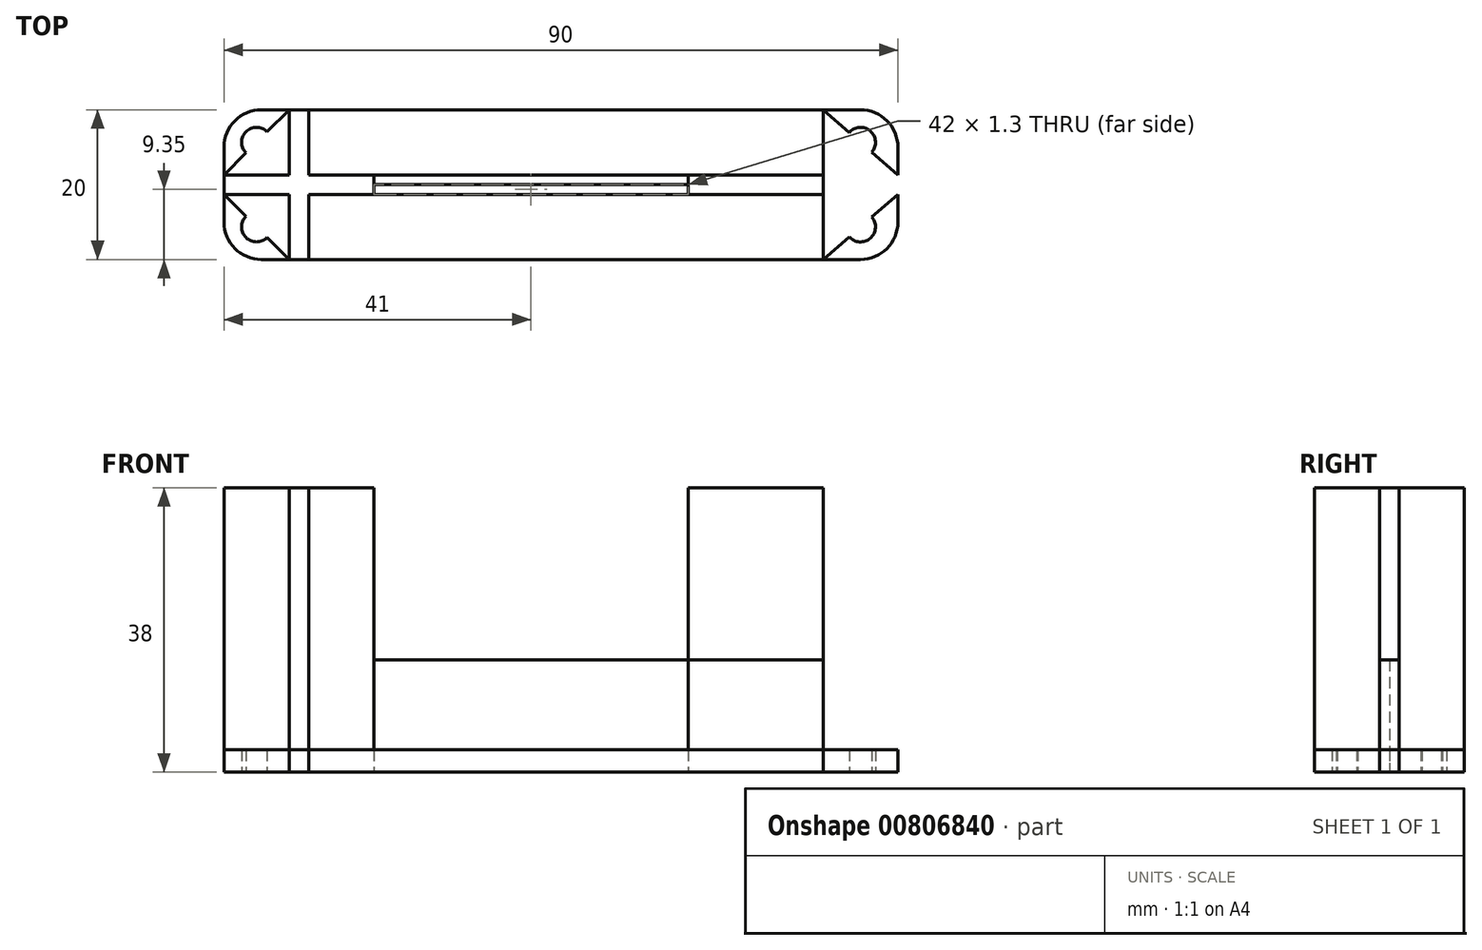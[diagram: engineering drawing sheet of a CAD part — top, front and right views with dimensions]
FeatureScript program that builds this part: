
annotation { "Feature Type Name" : "Feature", "Feature Type Description" : "" }
export const myFeature = defineFeature(function(context is Context, id is Id, definition is map)
    precondition{}
    {
        {
            var Q0;
            Q0=qCreatedBy(makeId("Top.planeOp"),FACE);
            var sketch = newSketch(context, id + "F0", { "sketchPlane" : qUnion([Q0])});
            skLineSegment(sketch, "E0.bottom", {"start": v(10, 1.3) * mm, "end": v(-10, 1.3) * mm});
            skLineSegment(sketch, "E0.top", {"start": v(10, -1.3) * mm, "end": v(-10, -1.3) * mm});
            skLineSegment(sketch, "E0.left", {"start": v(10, 1.3) * mm, "end": v(10, -1.3) * mm});
            skLineSegment(sketch, "E0.right", {"start": v(-10, 1.3) * mm, "end": v(-10, -1.3) * mm});
            skPoint(sketch, "E0.middle", {"position": v(0, 0) * mm});
            skLineSegment(sketch, "E1.bottom", {"start": v(1.3, 10) * mm, "end": v(-1.3, 10) * mm});
            skLineSegment(sketch, "E1.top", {"start": v(1.3, -10) * mm, "end": v(-1.3, -10) * mm});
            skLineSegment(sketch, "E1.left", {"start": v(1.3, 10) * mm, "end": v(1.3, -10) * mm});
            skLineSegment(sketch, "E1.right", {"start": v(-1.3, 10) * mm, "end": v(-1.3, -10) * mm});
            skLineSegment(sketch, "E2.bottom", {"start": v(0, 0) * mm, "end": v(80, 0) * mm});
            skLineSegment(sketch, "E2.top", {"start": v(0, 1.3) * mm, "end": v(80, 1.3) * mm});
            skLineSegment(sketch, "E2.left", {"start": v(0, 0) * mm, "end": v(0, 1.3) * mm});
            skLineSegment(sketch, "E2.right", {"start": v(80, 0) * mm, "end": v(80, 1.3) * mm});
            skLineSegment(sketch, "E3.top", {"start": v(0, -1.3) * mm, "end": v(80, -1.3) * mm});
            skLineSegment(sketch, "E3.left", {"start": v(0, 0) * mm, "end": v(0, -1.3) * mm});
            skLineSegment(sketch, "E3.right", {"start": v(80, 0) * mm, "end": v(80, -1.3) * mm});
            skLineSegment(sketch, "E4.bottom", {"start": v(-5, -10) * mm, "end": v(75, -10) * mm});
            skLineSegment(sketch, "E4.top", {"start": v(-5, 10) * mm, "end": v(75, 10) * mm});
            skLineSegment(sketch, "E4.left", {"start": v(-10, -5) * mm, "end": v(-10, 5) * mm});
            skLineSegment(sketch, "E4.right", {"start": v(80, -10) * mm, "end": v(80, 10) * mm});
            skLineSegment(sketch, "E5.bottom", {"start": v(80, -10) * mm, "end": v(70, -10) * mm});
            skLineSegment(sketch, "E5.top", {"start": v(80, 10) * mm, "end": v(70, 10) * mm});
            skLineSegment(sketch, "E5.left", {"start": v(80, -5) * mm, "end": v(80, 5) * mm});
            skLineSegment(sketch, "E5.right", {"start": v(70, -10) * mm, "end": v(70, 10) * mm});
            skArc(sketch, "E6", {"start": v(1.3, 10) * mm, "mid": v(35.65, 3.3) * mm, "end": v(70, 10) * mm});
            skArc(sketch, "E7", {"start": v(70, -10) * mm, "mid": v(35.65, -3.3) * mm, "end": v(1.3, -10) * mm});
            skLineSegment(sketch, "E8", {"start": v(35.65, -3.3) * mm, "end": v(35.65, -1.3) * mm});
            skLineSegment(sketch, "E9", {"start": v(35.65, 3.3) * mm, "end": v(35.65, 1.3) * mm});
            skLineSegment(sketch, "E10", {"start": v(-10, 1.3) * mm, "end": v(-1.3, 10) * mm});
            skCircle(sketch, "E11", {"center": v(-5.65, 5.65) * mm, "radius": 2 * mm});
            skLineSegment(sketch, "E12", {"start": v(-10, -1.3) * mm, "end": v(-1.3, -10) * mm});
            skLineSegment(sketch, "E13", {"start": v(70, 10) * mm, "end": v(80, 1.3) * mm});
            skLineSegment(sketch, "E14", {"start": v(70, -10) * mm, "end": v(80, -1.3) * mm});
            skCircle(sketch, "E15", {"center": v(-5.65, -5.65) * mm, "radius": 2 * mm});
            skPoint(sketch, "E16.visualSharp", {"position": v(-10, 10) * mm});
            skArc(sketch, "E16.filletArc", {"start": v(-5, 10) * mm, "mid": v(-8.54, 8.54) * mm, "end": v(-10, 5) * mm});
            skPoint(sketch, "E17.visualSharp", {"position": v(-10, -10) * mm});
            skArc(sketch, "E17.filletArc", {"start": v(-10, -5) * mm, "mid": v(-8.54, -8.54) * mm, "end": v(-5, -10) * mm});
            skCircle(sketch, "E18", {"center": v(75, 5.65) * mm, "radius": 2 * mm});
            skCircle(sketch, "E19", {"center": v(75, -5.65) * mm, "radius": 2 * mm});
            skPoint(sketch, "E20.visualSharp", {"position": v(80, 10) * mm});
            skArc(sketch, "E20.filletArc", {"start": v(80, 5) * mm, "mid": v(78.54, 8.54) * mm, "end": v(75, 10) * mm});
            skPoint(sketch, "E21.visualSharp", {"position": v(80, -10) * mm});
            skArc(sketch, "E21.filletArc", {"start": v(75, -10) * mm, "mid": v(78.54, -8.54) * mm, "end": v(80, -5) * mm});
            skLineSegment(sketch, "E22", {"start": v(0, -1.3) * mm, "end": v(52, -1.3) * mm});
            skLineSegment(sketch, "E23", {"start": v(52, -1.3) * mm, "end": v(52, 1.3) * mm});
            skSolve(sketch);
        }
        {
            var Q0;
            {var subQ0=sQuery(id+"F0.wireOp",EDGE,"E5.left");var subQ1=sQuery(id+"F0.wireOp",EDGE,"E2.bottom");var subQ2=makeQuery(id+"F0.imprint","INTERSECT",VERTEX,{"derivedFrom":[subQ1,subQ0]});Q0=makeQuery(id+"F0.imprint","IMPRINT",FACE,{"disambiguationData":[TD([[makeQuery(id+"F0.imprint","IMPRINT",EDGE,{"disambiguationData":[TD([[subQ2,1.0]])],"derivedFrom":subQ1}),-1.0]])]});}
            var Q1;
            {var subQ0=sQuery(id+"F0.wireOp",EDGE,"E5.left");var subQ5=sQuery(id+"F0.wireOp",EDGE,"E2.bottom");var subQ6=makeQuery(id+"F0.imprint","INTERSECT",VERTEX,{"derivedFrom":[subQ5,subQ0]});Q1=makeQuery(id+"F0.imprint","IMPRINT",FACE,{"disambiguationData":[TD([[makeQuery(id+"F0.imprint","IMPRINT",EDGE,{"disambiguationData":[TD([[subQ6,1.0]])],"derivedFrom":subQ5}),1.0]])]});}
            var Q2;
            {var subQ1=sQuery(id+"F0.wireOp",EDGE,"E0.bottom");var subQ7=sQuery(id+"F0.wireOp",EDGE,"E1.right");var subQ9=makeQuery(id+"F0.imprint","INTERSECT",VERTEX,{"derivedFrom":[subQ1,subQ7]});Q2=makeQuery(id+"F0.imprint","IMPRINT",FACE,{"disambiguationData":[TD([[makeQuery(id+"F0.imprint","IMPRINT",EDGE,{"disambiguationData":[TD([[subQ9,1.0]])],"derivedFrom":subQ1}),-1.0]])]});}
            var Q3;
            {var subQ1=sQuery(id+"F0.wireOp",EDGE,"E0.bottom");var subQ3=sQuery(id+"F0.wireOp",EDGE,"E1.right");var subQ4=makeQuery(id+"F0.imprint","INTERSECT",VERTEX,{"derivedFrom":[subQ1,subQ3]});Q3=makeQuery(id+"F0.imprint","IMPRINT",FACE,{"disambiguationData":[TD([[makeQuery(id+"F0.imprint","IMPRINT",EDGE,{"disambiguationData":[TD([[subQ4,-1.0]])],"derivedFrom":subQ3}),-1.0]])]});}
            var Q4;
            {var subQ3=sQuery(id+"F0.wireOp",EDGE,"E1.right");var subQ7=sQuery(id+"F0.wireOp",EDGE,"E0.top");var subQ8=makeQuery(id+"F0.imprint","INTERSECT",VERTEX,{"derivedFrom":[subQ7,subQ3]});Q4=makeQuery(id+"F0.imprint","IMPRINT",FACE,{"disambiguationData":[TD([[makeQuery(id+"F0.imprint","IMPRINT",EDGE,{"disambiguationData":[TD([[subQ8,1.0]])],"derivedFrom":subQ7}),1.0]])]});}
            var Q5;
            {var subQ0=sQuery(id+"F0.wireOp",EDGE,"E22");var subQ1=sQuery(id+"F0.wireOp",EDGE,"E0.left");var subQ2=makeQuery(id+"F0.imprint","INTERSECT",VERTEX,{"derivedFrom":[subQ1,subQ0]});Q5=makeQuery(id+"F0.imprint","IMPRINT",FACE,{"disambiguationData":[TD([[makeQuery(id+"F0.imprint","IMPRINT",EDGE,{"disambiguationData":[TD([[subQ2,1.0]])],"derivedFrom":subQ1}),-1.0]])]});}
            var Q6;
            {var subQ0=sQuery(id+"F0.wireOp",EDGE,"E2.top");var subQ1=sQuery(id+"F0.wireOp",EDGE,"E0.left");var subQ2=makeQuery(id+"F0.imprint","INTERSECT",VERTEX,{"derivedFrom":[subQ1,subQ0]});Q6=makeQuery(id+"F0.imprint","IMPRINT",FACE,{"disambiguationData":[TD([[makeQuery(id+"F0.imprint","IMPRINT",EDGE,{"disambiguationData":[TD([[subQ2,-1.0]])],"derivedFrom":subQ1}),-1.0]])]});}
            var Q7;
            {var subQ5=sQuery(id+"F0.wireOp",EDGE,"E3.left");Q7=makeQuery(id+"F0.imprint","IMPRINT",FACE,{"disambiguationData":[TD([[makeQuery(id+"F0.imprint","IMPRINT",EDGE,{"derivedFrom":subQ5}),1.0]])]});}
            var Q8;
            {var subQ5=sQuery(id+"F0.wireOp",EDGE,"E2.left");Q8=makeQuery(id+"F0.imprint","IMPRINT",FACE,{"disambiguationData":[TD([[makeQuery(id+"F0.imprint","IMPRINT",EDGE,{"derivedFrom":subQ5}),-1.0]])]});}
            var Q9;
            {var subQ0=sQuery(id+"F0.wireOp",EDGE,"E2.left");Q9=makeQuery(id+"F0.imprint","IMPRINT",FACE,{"disambiguationData":[TD([[makeQuery(id+"F0.imprint","IMPRINT",EDGE,{"derivedFrom":subQ0}),1.0]])]});}
            extrude(context, id + "F1", {"entities" : qUnion([Q0, Q1, Q2, Q3, Q4, Q5, Q6, Q7, Q8, Q9]), "depth" : 38 * mm, "offsetDistance" : 25 * mm});
        }
        {
            var Q0;
            {var subQ8=sQuery(id+"F0.wireOp",EDGE,"E17.filletArc");Q0=makeQuery(id+"F0.imprint","IMPRINT",FACE,{"disambiguationData":[TD([[makeQuery(id+"F0.imprint","IMPRINT",EDGE,{"derivedFrom":subQ8}),1.0]])]});}
            var Q1;
            {var subQ0=sQuery(id+"F0.wireOp",EDGE,"E7");var subQ4=makeQuery(id+"F0.imprint","INTERSECT",VERTEX,{"derivedFrom":[subQ0,sQuery(id+"F0.wireOp",EDGE,"E8")]});Q1=makeQuery(id+"F0.imprint","IMPRINT",FACE,{"disambiguationData":[TD([[makeQuery(id+"F0.imprint","IMPRINT",EDGE,{"disambiguationData":[TD([[subQ4,-1.0]])],"derivedFrom":subQ0}),1.0]])]});}
            var Q2;
            {var subQ8=sQuery(id+"F0.wireOp",EDGE,"E16.filletArc");Q2=makeQuery(id+"F0.imprint","IMPRINT",FACE,{"disambiguationData":[TD([[makeQuery(id+"F0.imprint","IMPRINT",EDGE,{"derivedFrom":subQ8}),1.0]])]});}
            var Q3;
            {var subQ0=sQuery(id+"F0.wireOp",EDGE,"E6");var subQ4=makeQuery(id+"F0.imprint","INTERSECT",VERTEX,{"derivedFrom":[subQ0,sQuery(id+"F0.wireOp",EDGE,"E9")]});Q3=makeQuery(id+"F0.imprint","IMPRINT",FACE,{"disambiguationData":[TD([[makeQuery(id+"F0.imprint","IMPRINT",EDGE,{"disambiguationData":[TD([[subQ4,1.0]])],"derivedFrom":subQ0}),1.0]])]});}
            var Q4;
            {var subQ1=sQuery(id+"F0.wireOp",EDGE,"E0.bottom");var subQ3=sQuery(id+"F0.wireOp",EDGE,"E1.right");var subQ4=makeQuery(id+"F0.imprint","INTERSECT",VERTEX,{"derivedFrom":[subQ1,subQ3]});Q4=makeQuery(id+"F0.imprint","IMPRINT",FACE,{"disambiguationData":[TD([[makeQuery(id+"F0.imprint","IMPRINT",EDGE,{"disambiguationData":[TD([[subQ4,-1.0]])],"derivedFrom":subQ3}),-1.0]])]});}
            var Q5;
            {var subQ0=sQuery(id+"F0.wireOp",EDGE,"E5.left");var subQ5=sQuery(id+"F0.wireOp",EDGE,"E2.bottom");var subQ6=makeQuery(id+"F0.imprint","INTERSECT",VERTEX,{"derivedFrom":[subQ5,subQ0]});Q5=makeQuery(id+"F0.imprint","IMPRINT",FACE,{"disambiguationData":[TD([[makeQuery(id+"F0.imprint","IMPRINT",EDGE,{"disambiguationData":[TD([[subQ6,1.0]])],"derivedFrom":subQ5}),1.0]])]});}
            var Q6;
            {var subQ0=sQuery(id+"F0.wireOp",EDGE,"E5.left");var subQ1=sQuery(id+"F0.wireOp",EDGE,"E2.bottom");var subQ2=makeQuery(id+"F0.imprint","INTERSECT",VERTEX,{"derivedFrom":[subQ1,subQ0]});Q6=makeQuery(id+"F0.imprint","IMPRINT",FACE,{"disambiguationData":[TD([[makeQuery(id+"F0.imprint","IMPRINT",EDGE,{"disambiguationData":[TD([[subQ2,1.0]])],"derivedFrom":subQ1}),-1.0]])]});}
            var Q7;
            {var subQ7=sQuery(id+"F0.wireOp",EDGE,"E21.filletArc");Q7=makeQuery(id+"F0.imprint","IMPRINT",FACE,{"disambiguationData":[TD([[makeQuery(id+"F0.imprint","IMPRINT",EDGE,{"derivedFrom":subQ7}),1.0]])]});}
            var Q8;
            {var subQ8=sQuery(id+"F0.wireOp",EDGE,"E20.filletArc");Q8=makeQuery(id+"F0.imprint","IMPRINT",FACE,{"disambiguationData":[TD([[makeQuery(id+"F0.imprint","IMPRINT",EDGE,{"derivedFrom":subQ8}),1.0]])]});}
            var Q9;
            {var subQ1=sQuery(id+"F0.wireOp",EDGE,"E0.bottom");var subQ7=sQuery(id+"F0.wireOp",EDGE,"E1.right");var subQ9=makeQuery(id+"F0.imprint","INTERSECT",VERTEX,{"derivedFrom":[subQ1,subQ7]});Q9=makeQuery(id+"F0.imprint","IMPRINT",FACE,{"disambiguationData":[TD([[makeQuery(id+"F0.imprint","IMPRINT",EDGE,{"disambiguationData":[TD([[subQ9,1.0]])],"derivedFrom":subQ1}),-1.0]])]});}
            var Q10;
            {var subQ0=sQuery(id+"F0.wireOp",EDGE,"E10");var subQ3=sQuery(id+"F0.wireOp",EDGE,"E11");var subQ7=makeQuery(id+"F0.imprint","INTERSECT",VERTEX,{"disambiguationData":[OD(0.0)],"derivedFrom":[subQ0,subQ3]});Q10=makeQuery(id+"F0.imprint","IMPRINT",FACE,{"disambiguationData":[TD([[makeQuery(id+"F0.imprint","IMPRINT",EDGE,{"disambiguationData":[TD([[subQ7,-1.0]])],"derivedFrom":subQ3}),-1.0]])]});}
            var Q11;
            {var subQ3=sQuery(id+"F0.wireOp",EDGE,"E1.right");var subQ7=sQuery(id+"F0.wireOp",EDGE,"E0.top");var subQ8=makeQuery(id+"F0.imprint","INTERSECT",VERTEX,{"derivedFrom":[subQ7,subQ3]});Q11=makeQuery(id+"F0.imprint","IMPRINT",FACE,{"disambiguationData":[TD([[makeQuery(id+"F0.imprint","IMPRINT",EDGE,{"disambiguationData":[TD([[subQ8,1.0]])],"derivedFrom":subQ7}),1.0]])]});}
            var Q12;
            {var subQ0=sQuery(id+"F0.wireOp",EDGE,"E12");var subQ3=sQuery(id+"F0.wireOp",EDGE,"E15");var subQ7=makeQuery(id+"F0.imprint","INTERSECT",VERTEX,{"disambiguationData":[OD(0.0)],"derivedFrom":[subQ0,subQ3]});Q12=makeQuery(id+"F0.imprint","IMPRINT",FACE,{"disambiguationData":[TD([[makeQuery(id+"F0.imprint","IMPRINT",EDGE,{"disambiguationData":[TD([[subQ7,1.0]])],"derivedFrom":subQ3}),-1.0]])]});}
            var Q13;
            {var subQ0=sQuery(id+"F0.wireOp",EDGE,"E13");var subQ3=sQuery(id+"F0.wireOp",EDGE,"E18");var subQ7=makeQuery(id+"F0.imprint","INTERSECT",VERTEX,{"disambiguationData":[OD(0.0)],"derivedFrom":[subQ0,subQ3]});Q13=makeQuery(id+"F0.imprint","IMPRINT",FACE,{"disambiguationData":[TD([[makeQuery(id+"F0.imprint","IMPRINT",EDGE,{"disambiguationData":[TD([[subQ7,-1.0]])],"derivedFrom":subQ3}),-1.0]])]});}
            var Q14;
            {var subQ0=sQuery(id+"F0.wireOp",EDGE,"E14");var subQ3=sQuery(id+"F0.wireOp",EDGE,"E19");var subQ8=makeQuery(id+"F0.imprint","INTERSECT",VERTEX,{"disambiguationData":[OD(0.0)],"derivedFrom":[subQ0,subQ3]});Q14=makeQuery(id+"F0.imprint","IMPRINT",FACE,{"disambiguationData":[TD([[makeQuery(id+"F0.imprint","IMPRINT",EDGE,{"disambiguationData":[TD([[subQ8,1.0]])],"derivedFrom":subQ3}),-1.0]])]});}
            var Q15;
            {var subQ4=sQuery(id+"F0.wireOp",EDGE,"E8");Q15=makeQuery(id+"F0.imprint","IMPRINT",FACE,{"disambiguationData":[TD([[makeQuery(id+"F0.imprint","IMPRINT",EDGE,{"derivedFrom":subQ4}),1.0]])]});}
            var Q16;
            {var subQ6=sQuery(id+"F0.wireOp",EDGE,"E9");Q16=makeQuery(id+"F0.imprint","IMPRINT",FACE,{"disambiguationData":[TD([[makeQuery(id+"F0.imprint","IMPRINT",EDGE,{"derivedFrom":subQ6}),1.0]])]});}
            var Q17;
            {var subQ2=sQuery(id+"F0.wireOp",EDGE,"E9");Q17=makeQuery(id+"F0.imprint","IMPRINT",FACE,{"disambiguationData":[TD([[makeQuery(id+"F0.imprint","IMPRINT",EDGE,{"derivedFrom":subQ2}),-1.0]])]});}
            var Q18;
            {var subQ1=sQuery(id+"F0.wireOp",EDGE,"E0.left");var subQ5=sQuery(id+"F0.wireOp",EDGE,"E2.top");var subQ8=makeQuery(id+"F0.imprint","INTERSECT",VERTEX,{"derivedFrom":[subQ1,subQ5]});Q18=makeQuery(id+"F0.imprint","IMPRINT",FACE,{"disambiguationData":[TD([[makeQuery(id+"F0.imprint","IMPRINT",EDGE,{"disambiguationData":[TD([[subQ8,-1.0]])],"derivedFrom":subQ1}),1.0]])]});}
            var Q19;
            {var subQ1=sQuery(id+"F0.wireOp",EDGE,"E22");var subQ4=sQuery(id+"F0.wireOp",EDGE,"E0.left");var subQ5=makeQuery(id+"F0.imprint","INTERSECT",VERTEX,{"derivedFrom":[subQ4,subQ1]});Q19=makeQuery(id+"F0.imprint","IMPRINT",FACE,{"disambiguationData":[TD([[makeQuery(id+"F0.imprint","IMPRINT",EDGE,{"disambiguationData":[TD([[subQ5,1.0]])],"derivedFrom":subQ4}),1.0]])]});}
            var Q20;
            {var subQ0=sQuery(id+"F0.wireOp",EDGE,"E23");var subQ1=sQuery(id+"F0.wireOp",EDGE,"E2.top");var subQ2=makeQuery(id+"F0.imprint","INTERSECT",VERTEX,{"derivedFrom":[subQ1,subQ0]});Q20=makeQuery(id+"F0.imprint","IMPRINT",FACE,{"disambiguationData":[TD([[makeQuery(id+"F0.imprint","IMPRINT",EDGE,{"disambiguationData":[TD([[subQ2,-1.0]])],"derivedFrom":subQ1}),-1.0]])]});}
            var Q21;
            {var subQ0=sQuery(id+"F0.wireOp",EDGE,"E2.top");var subQ1=sQuery(id+"F0.wireOp",EDGE,"E0.left");var subQ2=makeQuery(id+"F0.imprint","INTERSECT",VERTEX,{"derivedFrom":[subQ1,subQ0]});Q21=makeQuery(id+"F0.imprint","IMPRINT",FACE,{"disambiguationData":[TD([[makeQuery(id+"F0.imprint","IMPRINT",EDGE,{"disambiguationData":[TD([[subQ2,-1.0]])],"derivedFrom":subQ1}),-1.0]])]});}
            var Q22;
            {var subQ0=sQuery(id+"F0.wireOp",EDGE,"E22");var subQ1=sQuery(id+"F0.wireOp",EDGE,"E0.left");var subQ2=makeQuery(id+"F0.imprint","INTERSECT",VERTEX,{"derivedFrom":[subQ1,subQ0]});Q22=makeQuery(id+"F0.imprint","IMPRINT",FACE,{"disambiguationData":[TD([[makeQuery(id+"F0.imprint","IMPRINT",EDGE,{"disambiguationData":[TD([[subQ2,1.0]])],"derivedFrom":subQ1}),-1.0]])]});}
            var Q23;
            {var subQ5=sQuery(id+"F0.wireOp",EDGE,"E3.left");Q23=makeQuery(id+"F0.imprint","IMPRINT",FACE,{"disambiguationData":[TD([[makeQuery(id+"F0.imprint","IMPRINT",EDGE,{"derivedFrom":subQ5}),1.0]])]});}
            var Q24;
            {var subQ0=sQuery(id+"F0.wireOp",EDGE,"E2.left");Q24=makeQuery(id+"F0.imprint","IMPRINT",FACE,{"disambiguationData":[TD([[makeQuery(id+"F0.imprint","IMPRINT",EDGE,{"derivedFrom":subQ0}),1.0]])]});}
            var Q25;
            {var subQ5=sQuery(id+"F0.wireOp",EDGE,"E2.left");Q25=makeQuery(id+"F0.imprint","IMPRINT",FACE,{"disambiguationData":[TD([[makeQuery(id+"F0.imprint","IMPRINT",EDGE,{"derivedFrom":subQ5}),-1.0]])]});}
            var Q26;
            {var subQ0=sQuery(id+"F0.wireOp",EDGE,"E23");var subQ1=sQuery(id+"F0.wireOp",EDGE,"E2.bottom");var subQ2=makeQuery(id+"F0.imprint","INTERSECT",VERTEX,{"derivedFrom":[subQ1,subQ0]});Q26=makeQuery(id+"F0.imprint","IMPRINT",FACE,{"disambiguationData":[TD([[makeQuery(id+"F0.imprint","IMPRINT",EDGE,{"disambiguationData":[TD([[subQ2,-1.0]])],"derivedFrom":subQ1}),-1.0]])]});}
            var Q27;
            {var subQ3=sQuery(id+"F0.wireOp",EDGE,"E8");Q27=makeQuery(id+"F0.imprint","IMPRINT",FACE,{"disambiguationData":[TD([[makeQuery(id+"F0.imprint","IMPRINT",EDGE,{"derivedFrom":subQ3}),-1.0]])]});}
            extrude(context, id + "F2", {"entities" : qUnion([Q0, Q1, Q2, Q3, Q4, Q5, Q6, Q7, Q8, Q9, Q10, Q11, Q12, Q13, Q14, Q15, Q16, Q17, Q18, Q19, Q20, Q21, Q22, Q23, Q24, Q25, Q26, Q27]), "depth" : 3 * mm, "offsetDistance" : 25 * mm});
        }
        {
            var Q0;
            {var subQ1=sQuery(id+"F0.wireOp",EDGE,"E0.left");var subQ5=sQuery(id+"F0.wireOp",EDGE,"E2.top");var subQ8=makeQuery(id+"F0.imprint","INTERSECT",VERTEX,{"derivedFrom":[subQ1,subQ5]});Q0=makeQuery(id+"F0.imprint","IMPRINT",FACE,{"disambiguationData":[TD([[makeQuery(id+"F0.imprint","IMPRINT",EDGE,{"disambiguationData":[TD([[subQ8,-1.0]])],"derivedFrom":subQ1}),1.0]])]});}
            var Q1;
            {var subQ1=sQuery(id+"F0.wireOp",EDGE,"E22");var subQ4=sQuery(id+"F0.wireOp",EDGE,"E0.left");var subQ5=makeQuery(id+"F0.imprint","INTERSECT",VERTEX,{"derivedFrom":[subQ4,subQ1]});Q1=makeQuery(id+"F0.imprint","IMPRINT",FACE,{"disambiguationData":[TD([[makeQuery(id+"F0.imprint","IMPRINT",EDGE,{"disambiguationData":[TD([[subQ5,1.0]])],"derivedFrom":subQ4}),1.0]])]});}
            var Q2;
            {var subQ0=sQuery(id+"F0.wireOp",EDGE,"E23");var subQ1=sQuery(id+"F0.wireOp",EDGE,"E2.top");var subQ2=makeQuery(id+"F0.imprint","INTERSECT",VERTEX,{"derivedFrom":[subQ1,subQ0]});Q2=makeQuery(id+"F0.imprint","IMPRINT",FACE,{"disambiguationData":[TD([[makeQuery(id+"F0.imprint","IMPRINT",EDGE,{"disambiguationData":[TD([[subQ2,-1.0]])],"derivedFrom":subQ1}),-1.0]])]});}
            var Q3;
            {var subQ0=sQuery(id+"F0.wireOp",EDGE,"E23");var subQ1=sQuery(id+"F0.wireOp",EDGE,"E2.bottom");var subQ2=makeQuery(id+"F0.imprint","INTERSECT",VERTEX,{"derivedFrom":[subQ1,subQ0]});Q3=makeQuery(id+"F0.imprint","IMPRINT",FACE,{"disambiguationData":[TD([[makeQuery(id+"F0.imprint","IMPRINT",EDGE,{"disambiguationData":[TD([[subQ2,-1.0]])],"derivedFrom":subQ1}),-1.0]])]});}
            extrude(context, id + "F3", {"entities" : qUnion([Q0, Q1, Q2, Q3]), "depth" : 15 * mm, "offsetDistance" : 25 * mm});
        }
    });
